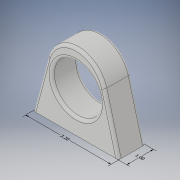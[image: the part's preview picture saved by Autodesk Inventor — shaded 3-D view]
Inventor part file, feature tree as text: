
AUTODESK INVENTOR PART (.ipt)
format: ipt  version: 2018 (Build 220112000, 112)  size: 182,272 bytes
history: native  units: in
note: dims shown in document units (in); Inventor stores cm internally (conversion verified against a paired STEP export)
features: other x5, extrude x3, sketch x3, chamfer x2, fillet x2
ambient origin geometry x8: Origin, YZ Plane, XZ Plane, XY Plane, X Axis, Y Axis, Z Axis, Center Point
bodies: Solid1 (feature_tree)
feature tree (15):
  other  "Annotations"
  extrude  "Extrusion1"  Depth=1.0in
  extrude  "Extrusion2"  Depth=1.0in
  chamfer  "Chamfer1"  Distance=1.0in
  chamfer  "Chamfer2"  Distance=0.8in Angle=45.0deg
  fillet  "Fillet1"  Radius=1.1in
  fillet  "Fillet2"  Radius=0.1in
  extrude  "Extrusion4"  Depth=1.0in
  sketch  "Sketch2"  dims[d2=3.2in d3=1.0in]
  sketch  "Sketch3"  dims[d4=3.0in d5=0.0in d6=1.8in d7=1.0in d8=0.0in d9=0.8in d10=3.0in d11=45.0deg]
  sketch  "Sketch5"  dims[d12=0.8in d13=3.0in d14=45.0deg d15=1.1in d16=0.1in d23=0.41in d24=0.24in d25=0.82in d26=0.48in d27=0.2in d28=0.0in d29=0.25in d30=0.2509in d31=0.82in d32=0.1756in d33=0.1228in d34=0.48in d35=0.1468in d36=0.1937in d37=3.2in d38=0.3269in d39=0.0268in d40=1.0in]
  other  "Linear Dimension 1"
  other  "Linear Dimension 2"
  other  "Linear Dimension 3"
  other  "Linear Dimension 4"
